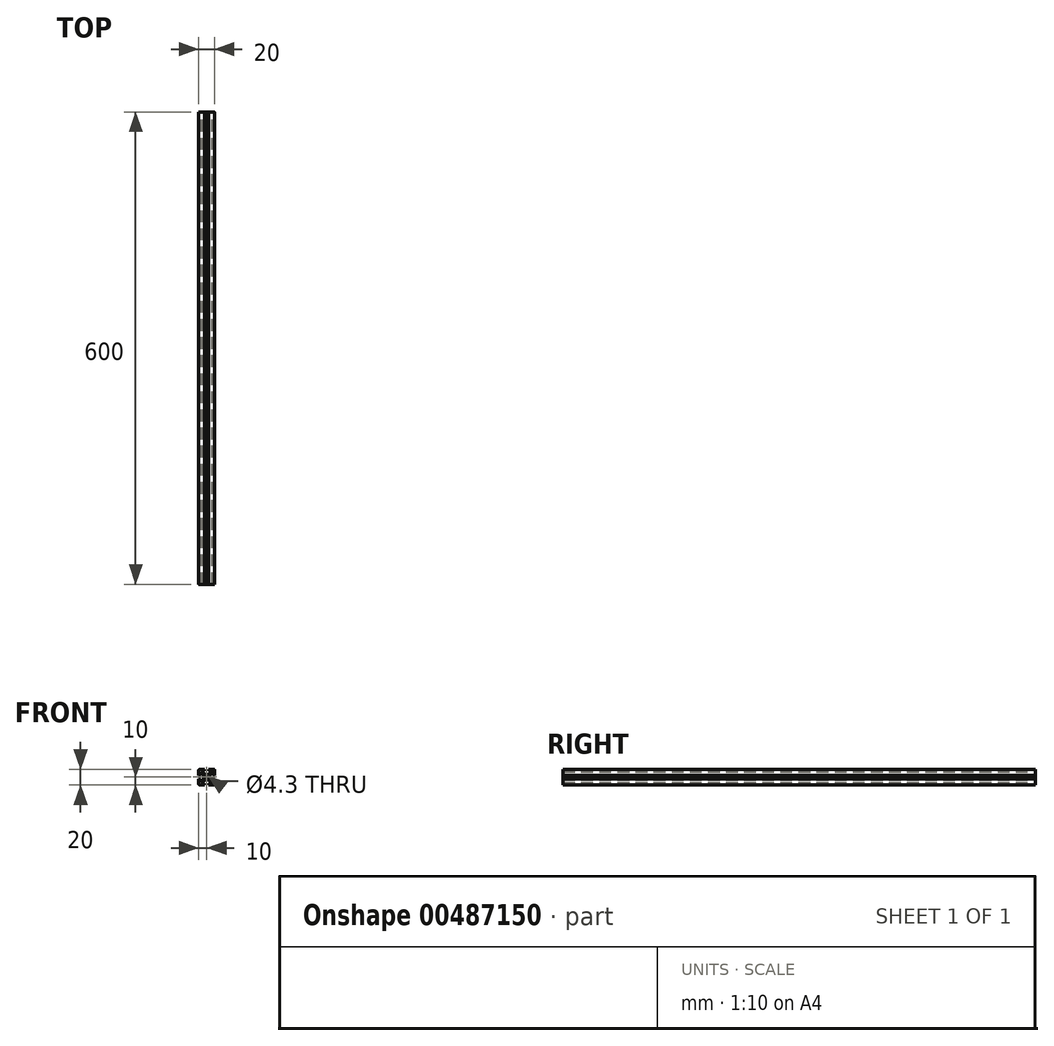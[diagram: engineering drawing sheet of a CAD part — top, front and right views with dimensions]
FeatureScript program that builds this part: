
annotation { "Feature Type Name" : "Feature", "Feature Type Description" : "" }
export const myFeature = defineFeature(function(context is Context, id is Id, definition is map)
    precondition{}
    {
        {
            var Q0;
            Q0=qCreatedBy(makeId("Front.planeOp"),FACE);
            var sketch = newSketch(context, id + "F0", { "sketchPlane" : qUnion([Q0])});
            skLineSegment(sketch, "E0.bottom", {"start": v(-10, 10) * mm, "end": v(-2.5, 10) * mm});
            skLineSegment(sketch, "E0.left", {"start": v(-10, 10) * mm, "end": v(-10, 2.5) * mm});
            skLineSegment(sketch, "E0.right", {"start": v(10, 10) * mm, "end": v(10, 2.5) * mm});
            skArc(sketch, "E1", {"start": v(2.15, 0) * mm, "mid": v(0, 2.15) * mm, "end": v(-2.15, 0) * mm});
            skLineSegment(sketch, "E2.bottom", {"start": v(-2.24, 3.65) * mm, "end": v(2.24, 3.65) * mm});
            skLineSegment(sketch, "E2.left", {"start": v(-3.65, 2.24) * mm, "end": v(-3.65, 0) * mm});
            skLineSegment(sketch, "E2.right", {"start": v(3.65, 2.24) * mm, "end": v(3.65, 0) * mm});
            skLineSegment(sketch, "E3", {"start": v(-2.5, 10) * mm, "end": v(-2.5, 8) * mm});
            skLineSegment(sketch, "E4", {"start": v(-2.5, 8) * mm, "end": v(-6.59, 8) * mm});
            skLineSegment(sketch, "E5", {"start": v(2.5, 10) * mm, "end": v(2.5, 8) * mm});
            skPoint(sketch, "E5.endSnap0", {"position": v(-6.25, 8) * mm});
            skLineSegment(sketch, "E6", {"start": v(2.5, 8) * mm, "end": v(6.59, 8) * mm});
            skLineSegment(sketch, "E7", {"start": v(-8, 6.59) * mm, "end": v(-8, 2.5) * mm});
            skLineSegment(sketch, "E8", {"start": v(-8, 2.5) * mm, "end": v(-10, 2.5) * mm});
            skLineSegment(sketch, "E9", {"start": v(-8, 6.59) * mm, "end": v(-3.65, 2.24) * mm});
            skLineSegment(sketch, "E10", {"start": v(-2.24, 3.65) * mm, "end": v(-6.59, 8) * mm});
            skPoint(sketch, "E10.endSnap0", {"position": v(-6.59, 0.05) * mm});
            skLineSegment(sketch, "E11", {"start": v(8, 6.59) * mm, "end": v(8, 2.5) * mm});
            skLineSegment(sketch, "E12", {"start": v(8, 2.5) * mm, "end": v(10, 2.5) * mm});
            skPoint(sketch, "E13.orphan", {"position": v(10, 8) * mm});
            skLineSegment(sketch, "E14", {"start": v(2.24, 3.65) * mm, "end": v(6.59, 8) * mm});
            skLineSegment(sketch, "E15", {"start": v(3.65, 2.24) * mm, "end": v(8, 6.59) * mm});
            skPoint(sketch, "E16.orphan", {"position": v(-10, 8) * mm});
            skPoint(sketch, "E17.orphan", {"position": v(-3.65, 3.65) * mm});
            skPoint(sketch, "E18.orphan", {"position": v(3.65, 3.65) * mm});
            skLineSegment(sketch, "E19", {"start": v(-10, 0) * mm, "end": v(10, 0) * mm, "construction": true});
            skPoint(sketch, "E0.top.end.orphan", {"position": v(10, -10) * mm});
            skPoint(sketch, "E0.top.start.orphan", {"position": v(-10, -10) * mm});
            skLineSegment(sketch, "E20.MirrorCS", {"start": v(-10, -10) * mm, "end": v(-10, -2.5) * mm});
            skLineSegment(sketch, "E21.MirrorCS", {"start": v(-8, -2.5) * mm, "end": v(-10, -2.5) * mm});
            skLineSegment(sketch, "E22.MirrorCS", {"start": v(-8, -6.59) * mm, "end": v(-8, -2.5) * mm});
            skLineSegment(sketch, "E23.MirrorCS", {"start": v(-8, -6.59) * mm, "end": v(-3.65, -2.24) * mm});
            skLineSegment(sketch, "E24.MirrorCS", {"start": v(-3.65, -2.24) * mm, "end": v(-3.65, 0) * mm});
            skArc(sketch, "E25.MirrorCS", {"start": v(2.15, 0) * mm, "mid": v(0, -2.15) * mm, "end": v(-2.15, 0) * mm});
            skLineSegment(sketch, "E26.MirrorCS", {"start": v(-2.24, -3.65) * mm, "end": v(-6.59, -8) * mm});
            skLineSegment(sketch, "E27.MirrorCS", {"start": v(-2.24, -3.65) * mm, "end": v(2.24, -3.65) * mm});
            skLineSegment(sketch, "E28.MirrorCS", {"start": v(-2.5, -8) * mm, "end": v(-6.59, -8) * mm});
            skLineSegment(sketch, "E29.MirrorCS", {"start": v(-2.5, -10) * mm, "end": v(-2.5, -8) * mm});
            skLineSegment(sketch, "E30.MirrorCS", {"start": v(-10, -10) * mm, "end": v(-2.5, -10) * mm});
            skLineSegment(sketch, "E31.MirrorCS", {"start": v(2.5, -10) * mm, "end": v(2.5, -8) * mm});
            skLineSegment(sketch, "E32.MirrorCS", {"start": v(2.5, -8) * mm, "end": v(6.59, -8) * mm});
            skLineSegment(sketch, "E33.MirrorCS", {"start": v(2.24, -3.65) * mm, "end": v(6.59, -8) * mm});
            skLineSegment(sketch, "E34.MirrorCS", {"start": v(3.65, -2.24) * mm, "end": v(8, -6.59) * mm});
            skLineSegment(sketch, "E35.MirrorCS", {"start": v(8, -6.59) * mm, "end": v(8, -2.5) * mm});
            skLineSegment(sketch, "E36.MirrorCS", {"start": v(8, -2.5) * mm, "end": v(10, -2.5) * mm});
            skLineSegment(sketch, "E37.MirrorCS", {"start": v(10, -10) * mm, "end": v(10, -2.5) * mm});
            skLineSegment(sketch, "E38.MirrorCS", {"start": v(3.65, -2.24) * mm, "end": v(3.65, 0) * mm});
            skLineSegment(sketch, "E39.trimOffspring", {"start": v(2.5, 10) * mm, "end": v(10, 10) * mm});
            skLineSegment(sketch, "E40.trimOffspring", {"start": v(2.5, -10) * mm, "end": v(10, -10) * mm});
            skSolve(sketch);
        }
        {
            var Q0;
            Q0 = qSketchRegion(id + "F0", true);
            extrude(context, id + "F1", {"entities" : qUnion([Q0]), "depth" : 300 * mm, "hasSecondDirection" : true, "secondDirectionOppositeDirection" : true, "secondDirectionDepth" : 300 * mm});
        }
        {
            var Q0;
            Q0=makeQuery(id+"F1.opExtrude","SWEPT_EDGE",EDGE,{"disambiguationData":[OSD([sQuery(id+"F0.wireOp",EDGE,"E0.bottom"),sQuery(id+"F0.wireOp",EDGE,"E0.left")])]});
            var Q1;
            Q1=makeQuery(id+"F1.opExtrude","SWEPT_EDGE",EDGE,{"disambiguationData":[OSD([sQuery(id+"F0.wireOp",EDGE,"E0.right"),sQuery(id+"F0.wireOp",EDGE,"E39.trimOffspring")])]});
            var Q2;
            Q2=makeQuery(id+"F1.opExtrude","SWEPT_EDGE",EDGE,{"disambiguationData":[OSD([sQuery(id+"F0.wireOp",EDGE,"E20.MirrorCS"),sQuery(id+"F0.wireOp",EDGE,"E30.MirrorCS")])]});
            var Q3;
            Q3=makeQuery(id+"F1.opExtrude","SWEPT_EDGE",EDGE,{"disambiguationData":[OSD([sQuery(id+"F0.wireOp",EDGE,"E37.MirrorCS"),sQuery(id+"F0.wireOp",EDGE,"E40.trimOffspring")])]});
            fillet(context, id + "F2", {"entities" : qUnion([Q0, Q1, Q2, Q3]), "radius" : 1 * mm, "tangentPropagation" : true, "allowEdgeOverflow" : false});
        }
    });
